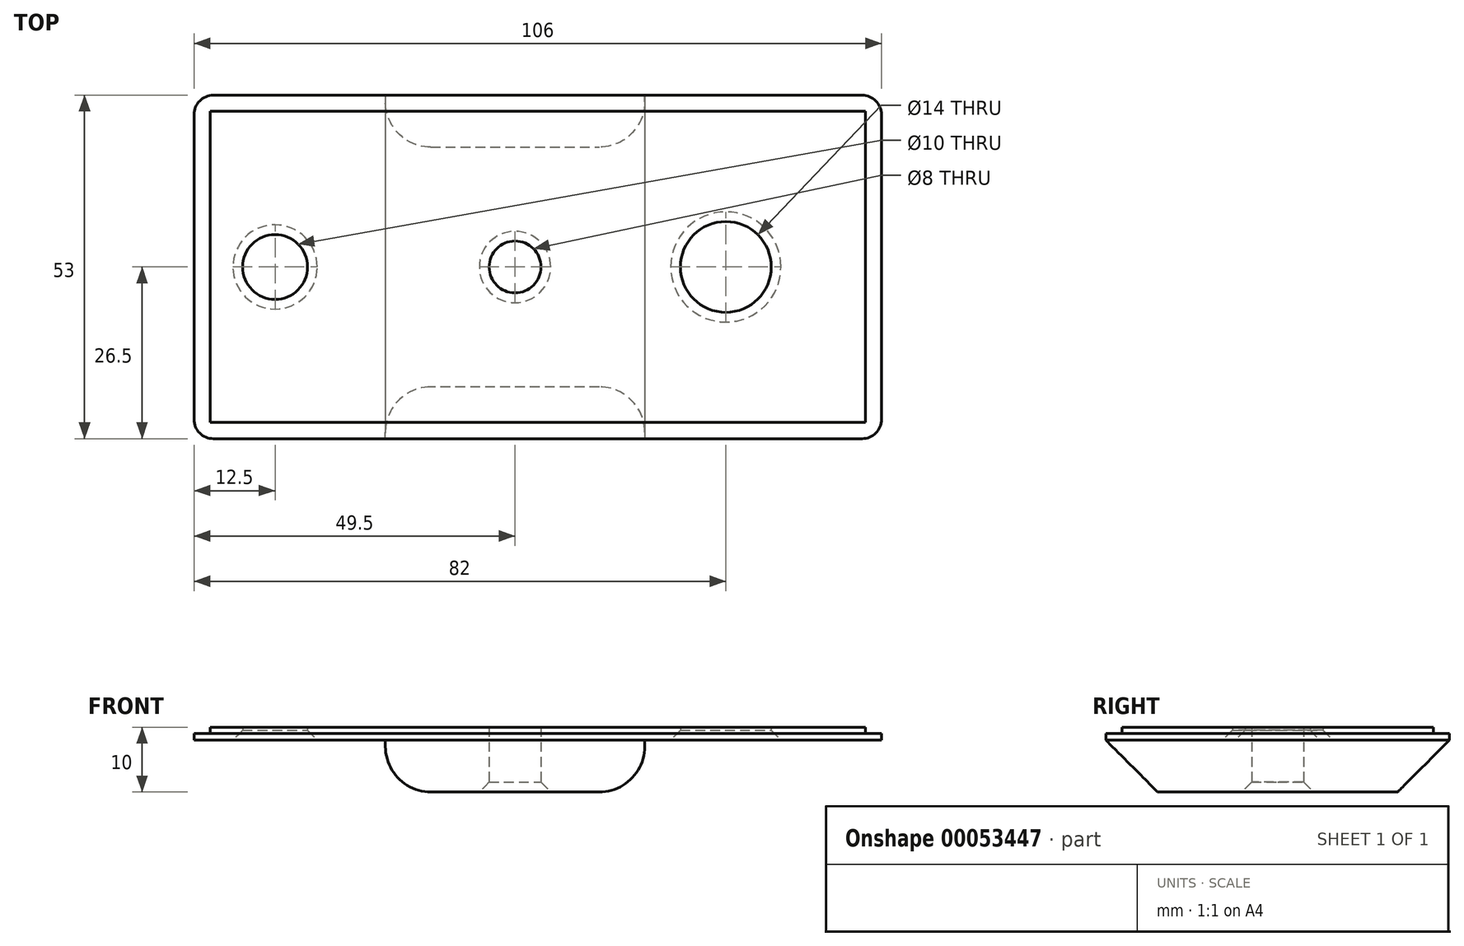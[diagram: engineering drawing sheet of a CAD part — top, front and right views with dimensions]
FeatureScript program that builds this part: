
annotation { "Feature Type Name" : "Feature", "Feature Type Description" : "" }
export const myFeature = defineFeature(function(context is Context, id is Id, definition is map)
    precondition{}
    {
        {
            var Q0;
            Q0=qCreatedBy(makeId("Top.planeOp"),FACE);
            var sketch = newSketch(context, id + "F0", { "sketchPlane" : qUnion([Q0])});
            skLineSegment(sketch, "E0.rect.bottom", {"start": v(53, -26.5) * mm, "end": v(-53, -26.5) * mm});
            skLineSegment(sketch, "E0.rect.top", {"start": v(53, 26.5) * mm, "end": v(-53, 26.5) * mm});
            skLineSegment(sketch, "E0.rect.left", {"start": v(53, -26.5) * mm, "end": v(53, 26.5) * mm});
            skLineSegment(sketch, "E0.rect.right", {"start": v(-53, -26.5) * mm, "end": v(-53, 26.5) * mm});
            skPoint(sketch, "E0.rect.middle", {"position": v(0, 0) * mm});
            skSolve(sketch);
        }
        {
            var Q0;
            Q0=makeQuery(id+"F0.imprint","IMPRINT",FACE,{"disambiguationData":[TD([[makeQuery(id+"F0.imprint","IMPRINT",EDGE,{"derivedFrom":sQuery(id+"F0.wireOp",EDGE,"E0.rect.bottom")}),-1.0]])]});
            extrude(context, id + "F1", {"entities" : qUnion([Q0]), "depth" : 1 * mm});
        }
        {
            var Q0;
            Q0=makeQuery(id+"F1.opExtrude","CAP_FACE",FACE,{"disambiguationData":[OSD([sQuery(id+"F0.wireOp",EDGE,"E0.rect.bottom"),sQuery(id+"F0.wireOp",EDGE,"E0.rect.top"),sQuery(id+"F0.wireOp",EDGE,"E0.rect.left"),sQuery(id+"F0.wireOp",EDGE,"E0.rect.right")])],"isStart":false});
            var sketch = newSketch(context, id + "F2", { "sketchPlane" : qUnion([Q0])});
            skLineSegment(sketch, "E1.rect.bottom", {"start": v(50.5, -24) * mm, "end": v(-50.5, -24) * mm});
            skLineSegment(sketch, "E1.rect.top", {"start": v(50.5, 24) * mm, "end": v(-50.5, 24) * mm});
            skLineSegment(sketch, "E1.rect.left", {"start": v(50.5, -24) * mm, "end": v(50.5, 24) * mm});
            skLineSegment(sketch, "E1.rect.right", {"start": v(-50.5, -24) * mm, "end": v(-50.5, 24) * mm});
            skPoint(sketch, "E1.rect.middle", {"position": v(0, 0) * mm});
            skSolve(sketch);
        }
        {
            var Q0;
            Q0=makeQuery(id+"F2.imprint","IMPRINT",FACE,{"disambiguationData":[TD([[makeQuery(id+"F2.imprint","IMPRINT",EDGE,{"derivedFrom":sQuery(id+"F2.wireOp",EDGE,"E1.rect.bottom")}),-1.0]])]});
            extrude(context, id + "F3", {"entities" : qUnion([Q0]), "operationType" : NewBodyOperationType.ADD, "depth" : 1 * mm});
        }
        {
            var Q0;
            Q0=makeQuery(id+"F1.opExtrude","SWEPT_EDGE",EDGE,{"disambiguationData":[OSD([sQuery(id+"F0.wireOp",EDGE,"E0.rect.bottom"),sQuery(id+"F0.wireOp",EDGE,"E0.rect.right")])]});
            var Q1;
            Q1=makeQuery(id+"F1.opExtrude","SWEPT_EDGE",EDGE,{"disambiguationData":[OSD([sQuery(id+"F0.wireOp",EDGE,"E0.rect.bottom"),sQuery(id+"F0.wireOp",EDGE,"E0.rect.left")])]});
            var Q2;
            Q2=makeQuery(id+"F1.opExtrude","SWEPT_EDGE",EDGE,{"disambiguationData":[OSD([sQuery(id+"F0.wireOp",EDGE,"E0.rect.top"),sQuery(id+"F0.wireOp",EDGE,"E0.rect.left")])]});
            var Q3;
            Q3=makeQuery(id+"F1.opExtrude","SWEPT_EDGE",EDGE,{"disambiguationData":[OSD([sQuery(id+"F0.wireOp",EDGE,"E0.rect.top"),sQuery(id+"F0.wireOp",EDGE,"E0.rect.right")])]});
            fillet(context, id + "F4", {"entities" : qUnion([Q0, Q1, Q2, Q3]), "radius" : 3 * mm, "tangentPropagation" : true, "allowEdgeOverflow" : false});
        }
        {
            var Q0;
            Q0=makeQuery(id+"F1.opExtrude","CAP_FACE",FACE,{"disambiguationData":[OSD([sQuery(id+"F0.wireOp",EDGE,"E0.rect.bottom"),sQuery(id+"F0.wireOp",EDGE,"E0.rect.top"),sQuery(id+"F0.wireOp",EDGE,"E0.rect.left"),sQuery(id+"F0.wireOp",EDGE,"E0.rect.right")])],"isStart":true});
            var sketch = newSketch(context, id + "F5", { "sketchPlane" : qUnion([Q0])});
            skLineSegment(sketch, "E2.0", {"start": v(-50.5, 24) * mm, "end": v(-50.5, -24) * mm, "construction": true});
            skLineSegment(sketch, "E2.1", {"start": v(50.5, -24) * mm, "end": v(-50.5, -24) * mm, "construction": true});
            skLineSegment(sketch, "E2.2", {"start": v(50.5, 24) * mm, "end": v(50.5, -24) * mm, "construction": true});
            skLineSegment(sketch, "E2.3", {"start": v(50.5, 24) * mm, "end": v(-50.5, 24) * mm, "construction": true});
            skLineSegment(sketch, "E3", {"start": v(-50.5, 0) * mm, "end": v(50.5, 0) * mm, "construction": true});
            skLineSegment(sketch, "E4.bottom", {"start": v(-50.5, 0) * mm, "end": v(-40.5, 0) * mm, "construction": true});
            skLineSegment(sketch, "E4.top", {"start": v(-50.5, -24) * mm, "end": v(-40.5, -24) * mm, "construction": true});
            skLineSegment(sketch, "E4.left", {"start": v(-50.5, 0) * mm, "end": v(-50.5, -24) * mm, "construction": true});
            skLineSegment(sketch, "E4.right", {"start": v(-40.5, 0) * mm, "end": v(-40.5, -24) * mm, "construction": true});
            skLineSegment(sketch, "E5.bottom", {"start": v(-50.5, 24) * mm, "end": v(-3.5, 24) * mm, "construction": true});
            skLineSegment(sketch, "E5.top", {"start": v(-50.5, 0) * mm, "end": v(-3.5, 0) * mm, "construction": true});
            skLineSegment(sketch, "E5.left", {"start": v(-50.5, 24) * mm, "end": v(-50.5, 0) * mm, "construction": true});
            skLineSegment(sketch, "E5.right", {"start": v(-3.5, 24) * mm, "end": v(-3.5, 0) * mm, "construction": true});
            skLineSegment(sketch, "E6.bottom", {"start": v(-50.5, 0) * mm, "end": v(29, 0) * mm, "construction": true});
            skLineSegment(sketch, "E6.top", {"start": v(-50.5, -24) * mm, "end": v(29, -24) * mm, "construction": true});
            skLineSegment(sketch, "E6.right", {"start": v(29, 0) * mm, "end": v(29, -24) * mm, "construction": true});
            skSolve(sketch);
        }
        {
            var Q0;
            Q0=sQuery(id+"F5.wireOp",VERTEX,"E6.bottom.end");
            var Q1;
            Q1=makeQuery(id+"F1.opExtrude","SWEPT_BODY",BODY,{"disambiguationData":[OSD([sQuery(id+"F0.wireOp",EDGE,"E0.rect.bottom"),sQuery(id+"F0.wireOp",EDGE,"E0.rect.top"),sQuery(id+"F0.wireOp",EDGE,"E0.rect.left"),sQuery(id+"F0.wireOp",EDGE,"E0.rect.right")])]});
            hole(context, id + "F6", {"style" : HoleStyle.C_SINK, "holeDiameter" : 14 * mm, "cSinkDiameter" : 17 * mm, "endStyle" : HoleEndStyle.THROUGH, "locations" : qUnion([Q0]), "scope" : qUnion([Q1]), "cSinkAngle" : 90 * degree, "isTappedThrough" : true});
        }
        {
            var Q0;
            Q0=sQuery(id+"F5.wireOp",VERTEX,"E4.bottom.end");
            var Q1;
            Q1=makeQuery(id+"F1.opExtrude","SWEPT_BODY",BODY,{"disambiguationData":[OSD([sQuery(id+"F0.wireOp",EDGE,"E0.rect.bottom"),sQuery(id+"F0.wireOp",EDGE,"E0.rect.top"),sQuery(id+"F0.wireOp",EDGE,"E0.rect.left"),sQuery(id+"F0.wireOp",EDGE,"E0.rect.right")])]});
            hole(context, id + "F7", {"style" : HoleStyle.C_SINK, "holeDiameter" : 10 * mm, "cSinkDiameter" : 13 * mm, "endStyle" : HoleEndStyle.THROUGH, "locations" : qUnion([Q0]), "scope" : qUnion([Q1]), "cSinkAngle" : 90 * degree, "isTappedThrough" : true});
        }
        {
            var Q0;
            {var subQ3=sQuery(id+"F0.wireOp",EDGE,"E0.rect.bottom");Q0=makeQuery(id+"F5.imprint","IMPRINT",FACE,{"disambiguationData":[TD([[makeQuery(id+"F5.imprint","IMPRINT",EDGE,{"derivedFrom":makeQuery(id+"F1.opExtrude","CAP_EDGE",EDGE,{"disambiguationData":[OSD([subQ3])],"isStart":true})}),1.0]])]});}
            var sketch = newSketch(context, id + "F8", { "sketchPlane" : qUnion([Q0])});
            skPoint(sketch, "E7.0", {"position": v(-3.5, 0) * mm});
            skLineSegment(sketch, "E8.bottom", {"start": v(16.5, -26.5) * mm, "end": v(-23.5, -26.5) * mm});
            skLineSegment(sketch, "E8.top", {"start": v(16.5, 26.5) * mm, "end": v(-23.5, 26.5) * mm});
            skLineSegment(sketch, "E8.left", {"start": v(16.5, -26.5) * mm, "end": v(16.5, 26.5) * mm});
            skLineSegment(sketch, "E8.right", {"start": v(-23.5, -26.5) * mm, "end": v(-23.5, 26.5) * mm});
            skSolve(sketch);
        }
        {
            var Q0;
            Q0 = qSketchRegion(id + "F8", true);
            extrude(context, id + "F9", {"entities" : qUnion([Q0]), "operationType" : NewBodyOperationType.ADD, "depth" : 8 * mm});
        }
        {
            var Q0;
            Q0=makeQuery(id+"F9.opExtrude","CAP_FACE",FACE,{"disambiguationData":[OSD([sQuery(id+"F8.wireOp",EDGE,"E8.bottom"),sQuery(id+"F8.wireOp",EDGE,"E8.top"),sQuery(id+"F8.wireOp",EDGE,"E8.left"),sQuery(id+"F8.wireOp",EDGE,"E8.right")])],"isStart":false});
            var sketch = newSketch(context, id + "F10", { "sketchPlane" : qUnion([Q0])});
            skPoint(sketch, "E9.0", {"position": v(-3.5, 0) * mm});
            skSolve(sketch);
        }
        {
            var Q0;
            Q0=sQuery(id+"F10.wireOp",VERTEX,"E9.0");
            var Q1;
            Q1=makeQuery(id+"F1.opExtrude","SWEPT_BODY",BODY,{"disambiguationData":[OSD([sQuery(id+"F0.wireOp",EDGE,"E0.rect.bottom"),sQuery(id+"F0.wireOp",EDGE,"E0.rect.top"),sQuery(id+"F0.wireOp",EDGE,"E0.rect.left"),sQuery(id+"F0.wireOp",EDGE,"E0.rect.right")])]});
            hole(context, id + "F11", {"style" : HoleStyle.C_SINK, "endStyle" : HoleEndStyle.THROUGH, "holeDiameter" : 8 * mm, "cSinkDiameter" : 11 * mm, "cSinkAngle" : 90 * degree, "locations" : qUnion([Q0]), "scope" : qUnion([Q1]), "isTappedThrough" : true});
        }
        {
            var Q0;
            Q0=makeQuery(id+"F9.opExtrude","CAP_EDGE",EDGE,{"disambiguationData":[OSD([sQuery(id+"F8.wireOp",EDGE,"E8.bottom")])],"isStart":false});
            var Q1;
            Q1=makeQuery(id+"F9.opExtrude","CAP_EDGE",EDGE,{"disambiguationData":[OSD([sQuery(id+"F8.wireOp",EDGE,"E8.top")])],"isStart":false});
            chamfer(context, id + "F12", {"entities" : qUnion([Q0, Q1]), "width" : 8 * mm, "tangentPropagation" : true});
        }
        {
            var Q0;
            Q0=makeQuery(id+"F9.opExtrude","CAP_EDGE",EDGE,{"disambiguationData":[OSD([sQuery(id+"F8.wireOp",EDGE,"E8.right")])],"isStart":false});
            var Q1;
            Q1=makeQuery(id+"F9.opExtrude","CAP_EDGE",EDGE,{"disambiguationData":[OSD([sQuery(id+"F8.wireOp",EDGE,"E8.left")])],"isStart":false});
            fillet(context, id + "F13", {"entities" : qUnion([Q0, Q1]), "radius" : 7 * mm, "tangentPropagation" : true, "allowEdgeOverflow" : false});
        }
    });
